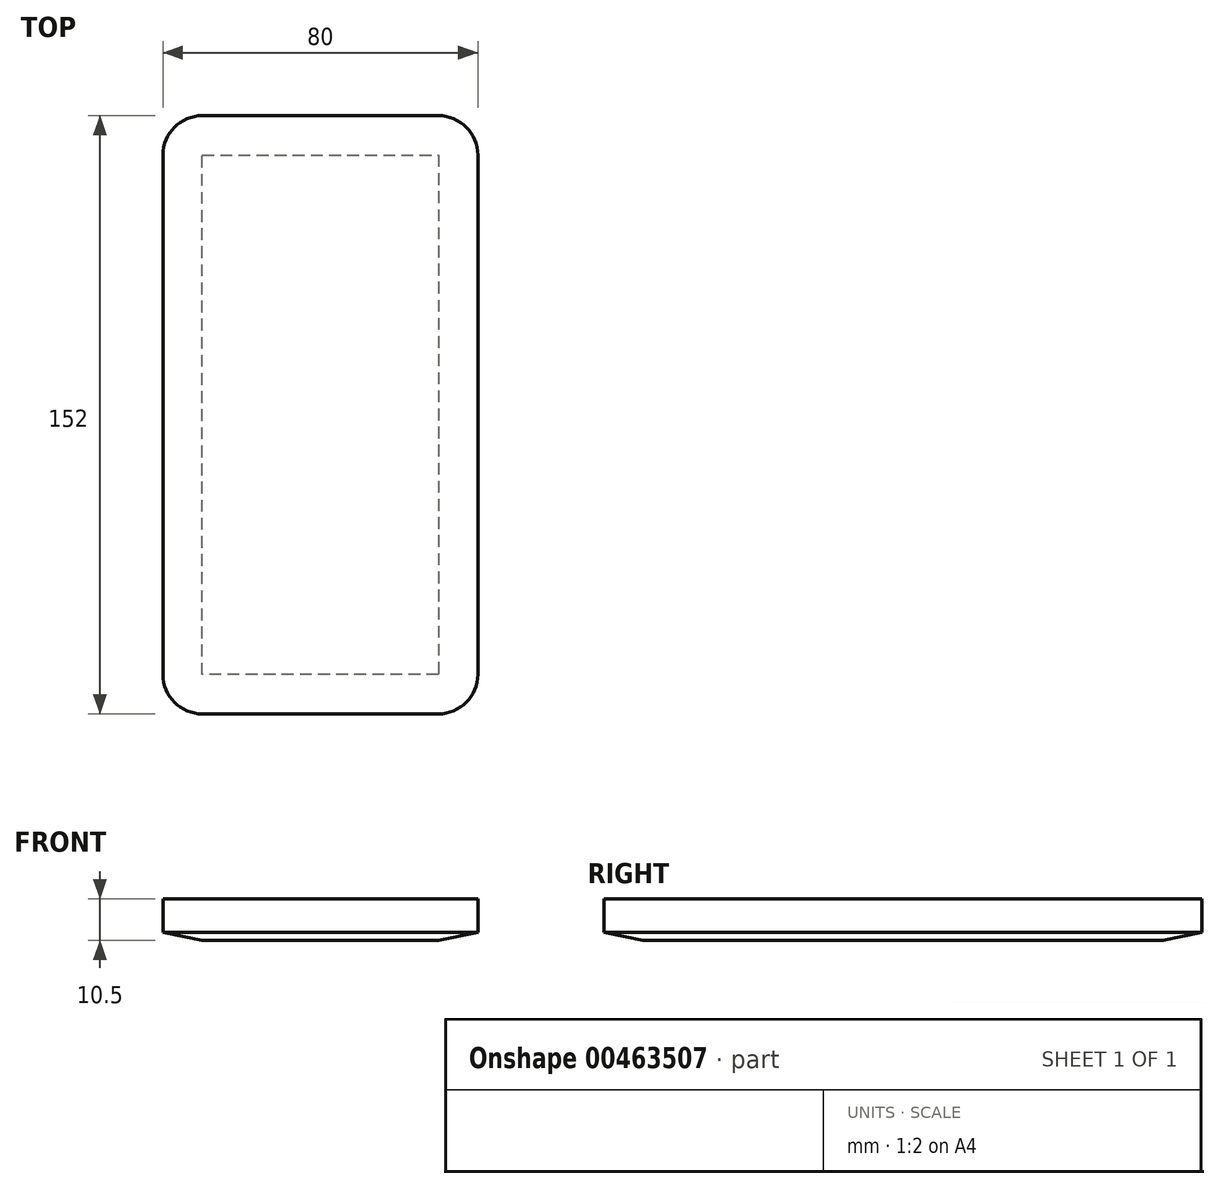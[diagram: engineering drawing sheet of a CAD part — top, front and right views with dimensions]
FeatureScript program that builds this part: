
annotation { "Feature Type Name" : "Feature", "Feature Type Description" : "" }
export const myFeature = defineFeature(function(context is Context, id is Id, definition is map)
    precondition{}
    {
        {
            var Q0;
            Q0=qCreatedBy(makeId("Top.planeOp"),FACE);
            var sketch = newSketch(context, id + "F0", { "sketchPlane" : qUnion([Q0])});
            skLineSegment(sketch, "E0.bottom", {"start": v(-40, 76) * mm, "end": v(40, 76) * mm});
            skLineSegment(sketch, "E0.top", {"start": v(-40, -76) * mm, "end": v(40, -76) * mm});
            skLineSegment(sketch, "E0.left", {"start": v(-40, 76) * mm, "end": v(-40, -76) * mm});
            skLineSegment(sketch, "E0.right", {"start": v(40, 76) * mm, "end": v(40, -76) * mm});
            skSolve(sketch);
        }
        {
            var Q0;
            Q0=makeQuery(id+"F0.imprint","IMPRINT",FACE,{"disambiguationData":[TD([[makeQuery(id+"F0.imprint","IMPRINT",EDGE,{"derivedFrom":sQuery(id+"F0.wireOp",EDGE,"E0.bottom")}),-1.0]])]});
            extrude(context, id + "F1", {"entities" : qUnion([Q0]), "depth" : 10.5 * mm});
        }
        {
            var Q0;
            Q0=makeQuery(id+"F1.opExtrude","SWEPT_EDGE",EDGE,{"disambiguationData":[OSD([sQuery(id+"F0.wireOp",EDGE,"E0.bottom"),sQuery(id+"F0.wireOp",EDGE,"E0.left")])]});
            var Q1;
            Q1=makeQuery(id+"F1.opExtrude","SWEPT_EDGE",EDGE,{"disambiguationData":[OSD([sQuery(id+"F0.wireOp",EDGE,"E0.bottom"),sQuery(id+"F0.wireOp",EDGE,"E0.right")])]});
            var Q2;
            Q2=makeQuery(id+"F1.opExtrude","SWEPT_EDGE",EDGE,{"disambiguationData":[OSD([sQuery(id+"F0.wireOp",EDGE,"E0.top"),sQuery(id+"F0.wireOp",EDGE,"E0.right")])]});
            var Q3;
            Q3=makeQuery(id+"F1.opExtrude","SWEPT_EDGE",EDGE,{"disambiguationData":[OSD([sQuery(id+"F0.wireOp",EDGE,"E0.top"),sQuery(id+"F0.wireOp",EDGE,"E0.left")])]});
            fillet(context, id + "F2", {"entities" : qUnion([Q0, Q1, Q2, Q3]), "radius" : 10 * mm, "tangentPropagation" : true, "allowEdgeOverflow" : false});
        }
        {
            var Q0;
            Q0=makeQuery(id+"F1.opExtrude","CAP_EDGE",EDGE,{"disambiguationData":[OSD([sQuery(id+"F0.wireOp",EDGE,"E0.bottom")])],"isStart":true});
            chamfer(context, id + "F3", {"entities" : qUnion([Q0]), "chamferType" : ChamferType.TWO_OFFSETS, "width1" : 10 * mm, "oppositeDirection" : false, "width2" : 2 * mm, "tangentPropagation" : true});
        }
    });
